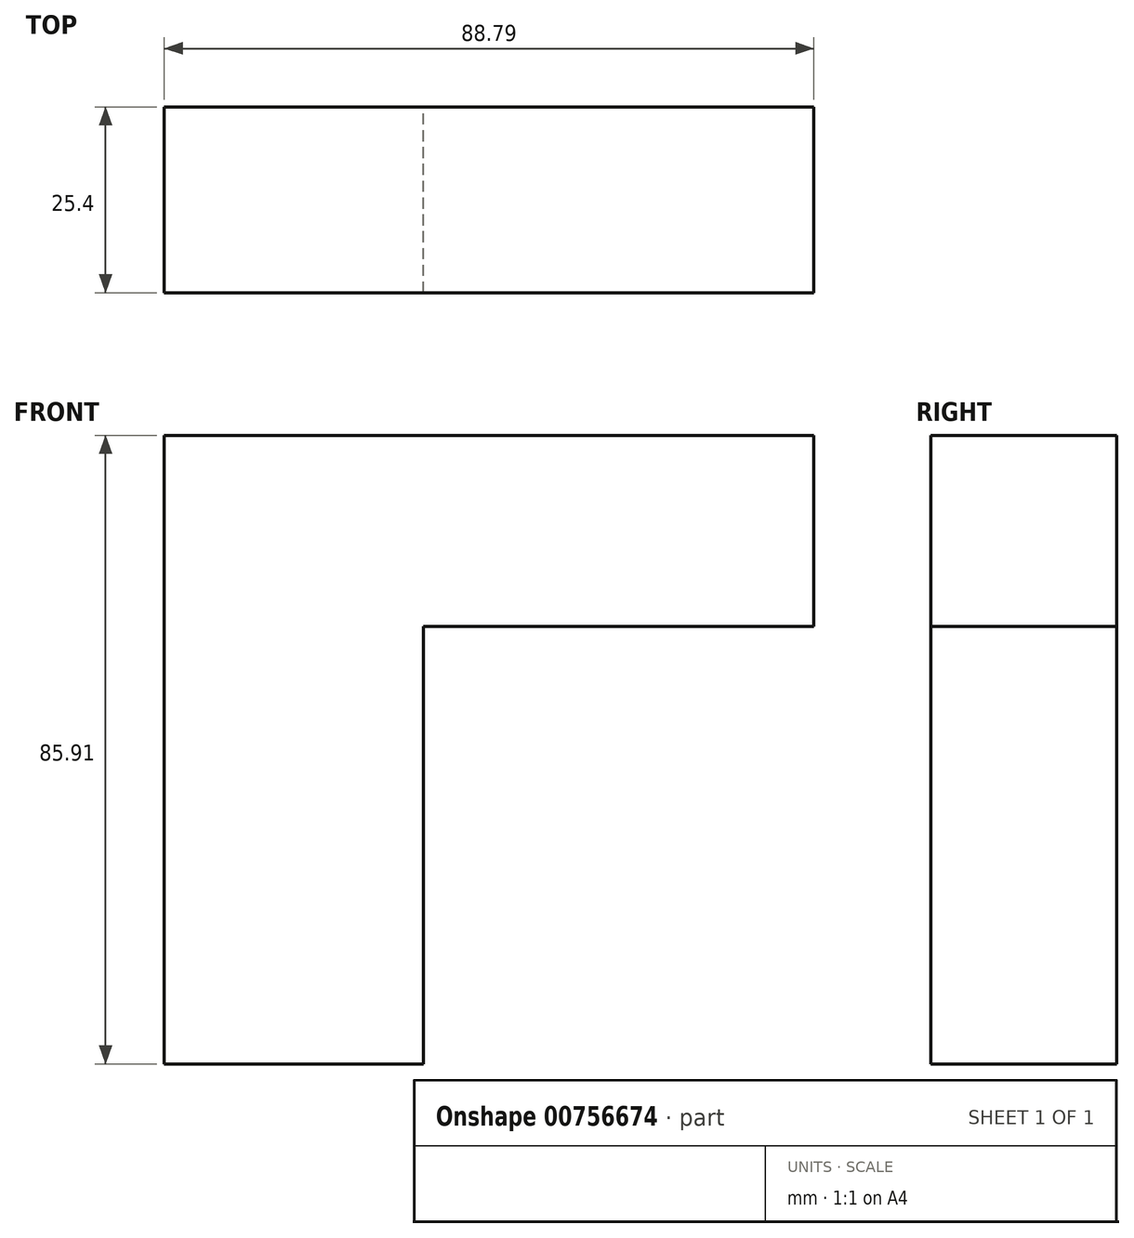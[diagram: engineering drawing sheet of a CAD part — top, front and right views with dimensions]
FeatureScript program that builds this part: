
annotation { "Feature Type Name" : "Feature", "Feature Type Description" : "" }
export const myFeature = defineFeature(function(context is Context, id is Id, definition is map)
    precondition{}
    {
        {
            var Q0;
            Q0=qCreatedBy(makeId("Front.planeOp"),FACE);
            var sketch = newSketch(context, id + "F0", { "sketchPlane" : qUnion([Q0])});
            skLineSegment(sketch, "E0", {"start": v(37.27, 48.63) * mm, "end": v(-51.52, 48.63) * mm});
            skLineSegment(sketch, "E1", {"start": v(-51.52, 48.63) * mm, "end": v(-51.52, -37.28) * mm});
            skLineSegment(sketch, "E2", {"start": v(-51.52, -37.28) * mm, "end": v(-16.07, -37.28) * mm});
            skLineSegment(sketch, "E3", {"start": v(-16.07, -37.28) * mm, "end": v(-16.07, 22.52) * mm});
            skLineSegment(sketch, "E4", {"start": v(-16.07, 22.52) * mm, "end": v(37.27, 22.52) * mm});
            skLineSegment(sketch, "E5", {"start": v(37.27, 22.52) * mm, "end": v(37.27, 48.63) * mm});
            skSolve(sketch);
        }
        {
            var Q0;
            Q0 = qSketchRegion(id + "F0", true);
            extrude(context, id + "F1", {"entities" : qUnion([Q0]), "depth" : 25.4 * mm, "offsetDistance" : 25.4 * mm});
        }
    });
